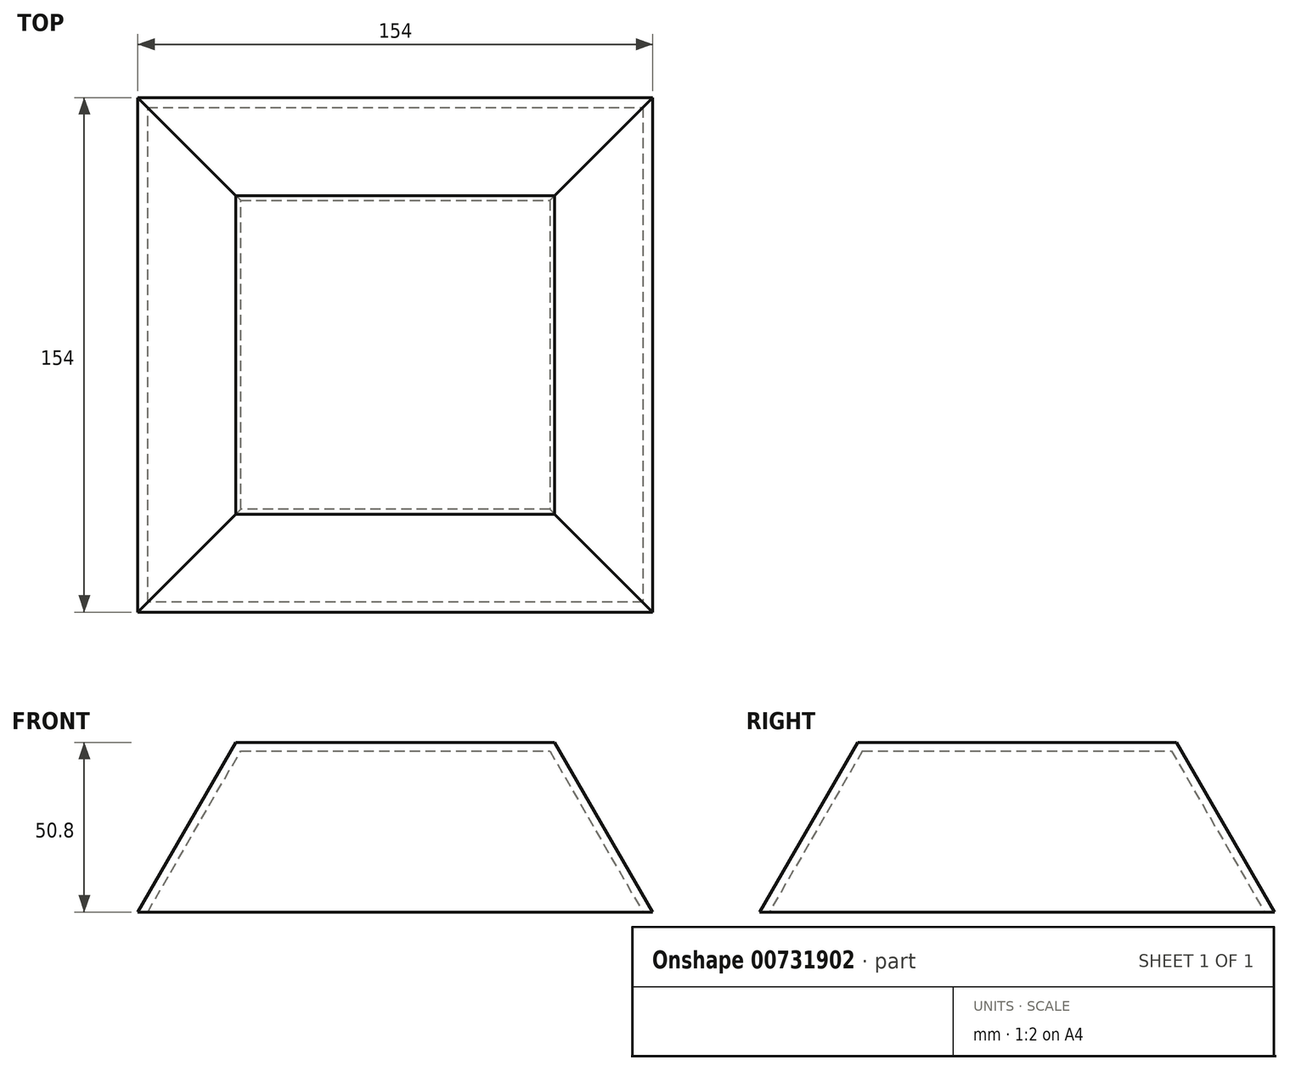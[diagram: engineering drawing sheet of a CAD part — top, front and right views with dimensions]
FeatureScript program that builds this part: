
annotation { "Feature Type Name" : "Feature", "Feature Type Description" : "" }
export const myFeature = defineFeature(function(context is Context, id is Id, definition is map)
    precondition{}
    {
        {
            var Q0;
            Q0=qCreatedBy(makeId("Top.planeOp"),FACE);
            var sketch = newSketch(context, id + "F0", { "sketchPlane" : qUnion([Q0])});
            skLineSegment(sketch, "E0.bottom", {"start": v(-77, 77) * mm, "end": v(77, 77) * mm});
            skLineSegment(sketch, "E0.top", {"start": v(-77, -77) * mm, "end": v(77, -77) * mm});
            skLineSegment(sketch, "E0.left", {"start": v(-77, 77) * mm, "end": v(-77, -77) * mm});
            skLineSegment(sketch, "E0.right", {"start": v(77, 77) * mm, "end": v(77, -77) * mm});
            skPoint(sketch, "E0.middle", {"position": v(0, 0) * mm});
            skSolve(sketch);
        }
        {
            var Q0;
            Q0=makeQuery(id+"F0.imprint","IMPRINT",FACE,{"disambiguationData":[TD([[makeQuery(id+"F0.imprint","IMPRINT",EDGE,{"derivedFrom":sQuery(id+"F0.wireOp",EDGE,"E0.bottom")}),-1.0]])]});
            extrude(context, id + "F1", {"entities" : qUnion([Q0]), "depth" : 50.8 * mm, "offsetDistance" : 25.4 * mm, "hasDraft" : true, "draftAngle" : 30 * degree, "draftPullDirection" : true});
        }
        {
            var Q0;
            Q0=makeQuery(id+"F1.opExtrude","CAP_FACE",FACE,{"disambiguationData":[OSD([sQuery(id+"F0.wireOp",EDGE,"E0.bottom"),sQuery(id+"F0.wireOp",EDGE,"E0.top"),sQuery(id+"F0.wireOp",EDGE,"E0.left"),sQuery(id+"F0.wireOp",EDGE,"E0.right")])],"isStart":true});
            shell(context, id + "F2", {"entities" : qUnion([Q0]), "thickness" : 2.54 * mm});
        }
    });
